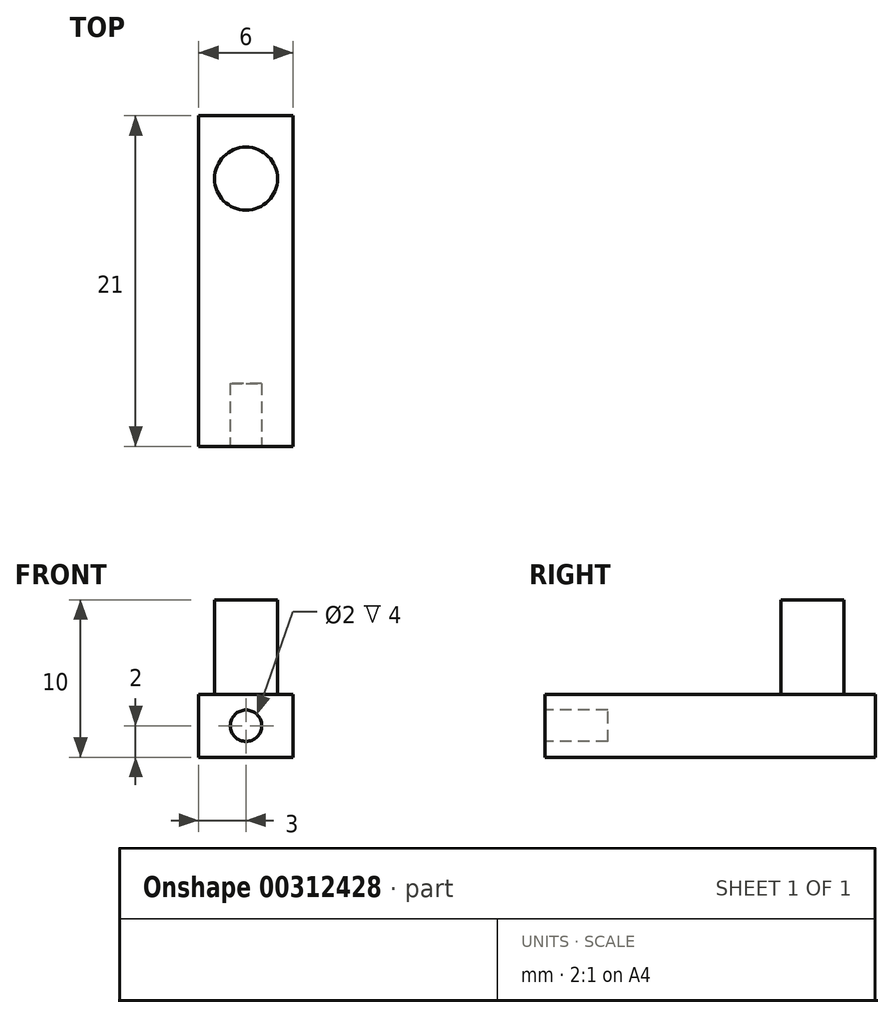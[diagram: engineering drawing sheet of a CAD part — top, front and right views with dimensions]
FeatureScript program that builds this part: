
annotation { "Feature Type Name" : "Feature", "Feature Type Description" : "" }
export const myFeature = defineFeature(function(context is Context, id is Id, definition is map)
    precondition{}
    {
        {
            var Q0;
            Q0=qCreatedBy(makeId("Top.planeOp"),FACE);
            var sketch = newSketch(context, id + "F0", { "sketchPlane" : qUnion([Q0])});
            skLineSegment(sketch, "E0.bottom", {"start": v(-6, 21) * mm, "end": v(0, 21) * mm});
            skLineSegment(sketch, "E0.top", {"start": v(-6, 0) * mm, "end": v(0, 0) * mm});
            skLineSegment(sketch, "E0.left", {"start": v(-6, 21) * mm, "end": v(-6, 0) * mm});
            skLineSegment(sketch, "E0.right", {"start": v(0, 21) * mm, "end": v(0, 0) * mm});
            skSolve(sketch);
        }
        {
            var Q0;
            Q0 = qSketchRegion(id + "F0", true);
            extrude(context, id + "F1", {"entities" : qUnion([Q0]), "depth" : 4 * mm});
        }
        {
            var Q0;
            Q0=makeQuery(id+"F1.opExtrude","CAP_FACE",FACE,{"disambiguationData":[OSD([sQuery(id+"F0.wireOp",EDGE,"E0.bottom"),sQuery(id+"F0.wireOp",EDGE,"E0.top"),sQuery(id+"F0.wireOp",EDGE,"E0.left"),sQuery(id+"F0.wireOp",EDGE,"E0.right")])],"isStart":false});
            var sketch = newSketch(context, id + "F2", { "sketchPlane" : qUnion([Q0])});
            skCircle(sketch, "E1", {"center": v(-3, 17) * mm, "radius": 2 * mm});
            skSolve(sketch);
        }
        {
            var Q0;
            Q0 = qSketchRegion(id + "F2", true);
            extrude(context, id + "F3", {"entities" : qUnion([Q0]), "operationType" : NewBodyOperationType.ADD, "depth" : 6 * mm});
        }
        {
            var Q0;
            Q0=makeQuery(id+"F1.opExtrude","SWEPT_FACE",FACE,{"disambiguationData":[OSD([sQuery(id+"F0.wireOp",EDGE,"E0.top")])]});
            var sketch = newSketch(context, id + "F4", { "sketchPlane" : qUnion([Q0])});
            skLineSegment(sketch, "E2", {"start": v(-3, 4) * mm, "end": v(-3, 0) * mm, "construction": true});
            skCircle(sketch, "E3", {"center": v(-3, 2) * mm, "radius": 1 * mm});
            skSolve(sketch);
        }
        {
            var Q0;
            Q0 = qSketchRegion(id + "F4", true);
            extrude(context, id + "F5", {"entities" : qUnion([Q0]), "operationType" : NewBodyOperationType.REMOVE, "oppositeDirection" : true, "depth" : 4 * mm});
        }
    });
